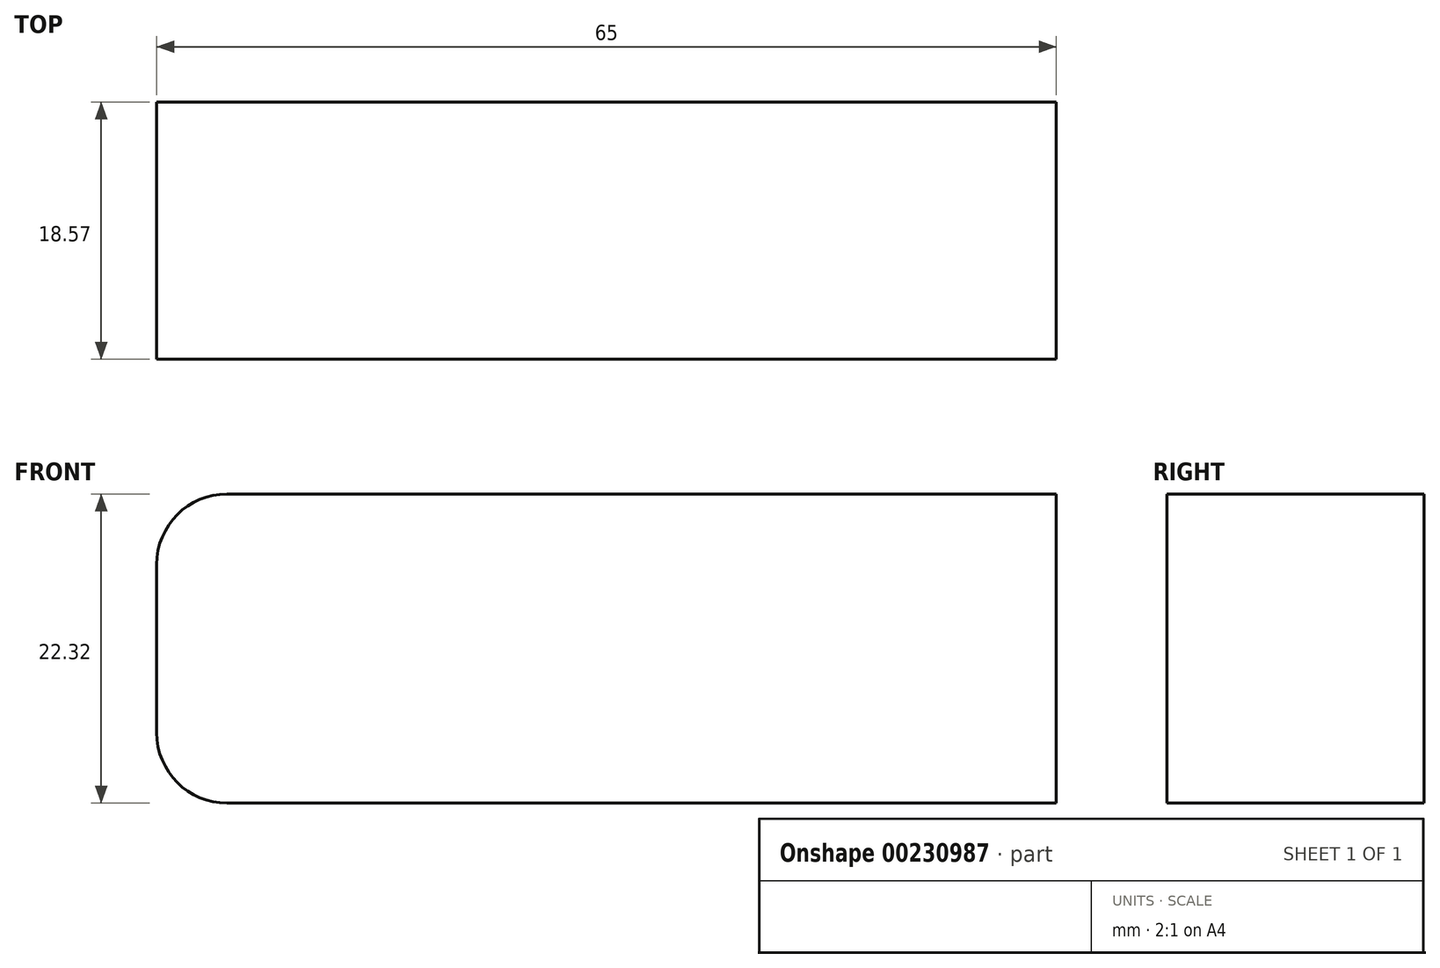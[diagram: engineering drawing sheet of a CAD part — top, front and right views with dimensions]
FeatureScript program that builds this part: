
annotation { "Feature Type Name" : "Feature", "Feature Type Description" : "" }
export const myFeature = defineFeature(function(context is Context, id is Id, definition is map)
    precondition{}
    {
        {
            var Q0;
            Q0=qCreatedBy(makeId("Front.planeOp"),FACE);
            var sketch = newSketch(context, id + "F0", { "sketchPlane" : qUnion([Q0])});
            skLineSegment(sketch, "E0.bottom", {"start": v(32.5, -11.16) * mm, "end": v(-32.5, -11.16) * mm});
            skLineSegment(sketch, "E0.top", {"start": v(32.5, 11.16) * mm, "end": v(-32.5, 11.16) * mm});
            skLineSegment(sketch, "E0.left", {"start": v(32.5, -11.16) * mm, "end": v(32.5, 11.16) * mm});
            skLineSegment(sketch, "E0.right", {"start": v(-32.5, -11.16) * mm, "end": v(-32.5, 11.16) * mm});
            skPoint(sketch, "E0.middle", {"position": v(0, 0) * mm});
            skSolve(sketch);
        }
        {
            var Q0;
            Q0 = qSketchRegion(id + "F0", true);
            extrude(context, id + "F1", {"entities" : qUnion([Q0]), "depth" : 18.57 * mm});
        }
        {
            var Q0;
            Q0=makeQuery(id+"F1.opExtrude","SWEPT_EDGE",EDGE,{"disambiguationData":[OSD([sQuery(id+"F0.wireOp",EDGE,"E0.top"),sQuery(id+"F0.wireOp",EDGE,"E0.right")])]});
            var Q1;
            Q1=makeQuery(id+"F1.opExtrude","SWEPT_EDGE",EDGE,{"disambiguationData":[OSD([sQuery(id+"F0.wireOp",EDGE,"E0.bottom"),sQuery(id+"F0.wireOp",EDGE,"E0.right")])]});
            fillet(context, id + "F2", {"entities" : qUnion([Q0, Q1]), "radius" : 5.08 * mm, "tangentPropagation" : true, "allowEdgeOverflow" : false});
        }
    });
